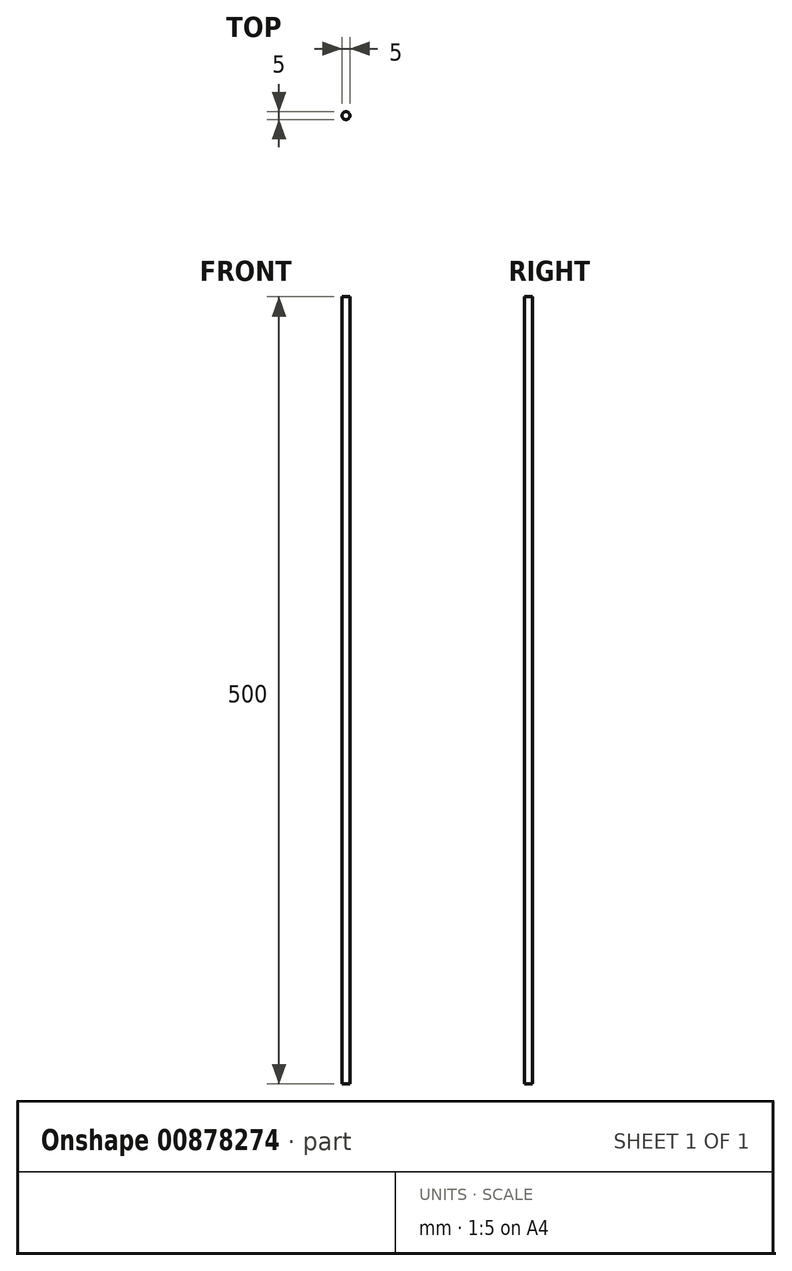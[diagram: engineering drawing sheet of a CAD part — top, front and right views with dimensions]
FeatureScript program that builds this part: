
annotation { "Feature Type Name" : "Feature", "Feature Type Description" : "" }
export const myFeature = defineFeature(function(context is Context, id is Id, definition is map)
    precondition{}
    {
        {
            var Q0;
            Q0=qCreatedBy(makeId("Top.planeOp"),FACE);
            var sketch = newSketch(context, id + "F0", { "sketchPlane" : qUnion([Q0])});
            skCircle(sketch, "E0", {"center": v(0, 0) * mm, "radius": 2.5 * mm});
            skSolve(sketch);
        }
        {
            var Q0;
            Q0 = qSketchRegion(id + "F0", true);
            extrude(context, id + "F1", {"entities" : qUnion([Q0]), "endBound" : BoundingType.SYMMETRIC, "depth" : 500 * mm, "offsetDistance" : 25 * mm});
        }
    });
